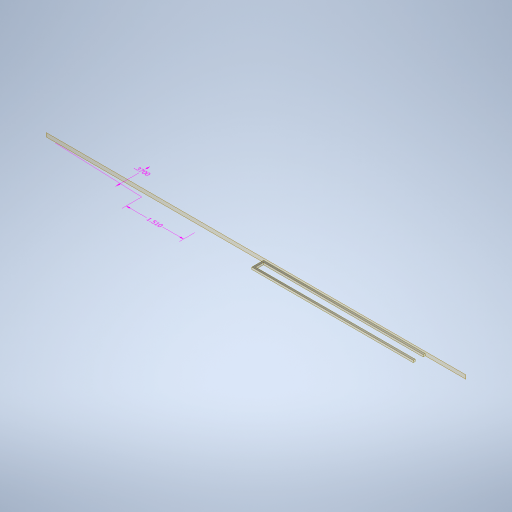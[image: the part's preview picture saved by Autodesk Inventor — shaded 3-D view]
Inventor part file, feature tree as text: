
AUTODESK INVENTOR PART (.ipt)
format: ipt  version: 2024.2 (Build 282272000, 272)  size: 276,992 bytes
history: native  units: in
note: dims shown in document units (in); Inventor stores cm internally (conversion verified against a paired STEP export)
features: other x3, plane x3, sketch x2, sweep x1
ambient origin geometry x8: Origin, YZ Plane, XZ Plane, XY Plane, X Axis, Y Axis, Z Axis, Center Point
bodies: Solid1 (feature_tree)
feature tree (9):
  other  "Annotations"
  sweep  "Sweep1"
  plane  "Work Plane1"
  plane  "Work Plane2"
  plane  "Work Plane4"
  sketch  "Sketch1"  dims[d6=0.0in d7=0.0in d11=0.25in d19=-0.25in]
  sketch  "Sketch2"  dims[d69=1.625in d70=1.625in d86=-0.1175in d89=0.1in d90=0.0in d91=0.0in d92=0.0in d98=0.02in d99=0.02in d42=0.2341in d43=0.169in d44=0.37in d48=0.2141in d49=0.2512in d50=1.51in]
  other  "Linear Dimension 1"
  other  "Linear Dimension 3"
